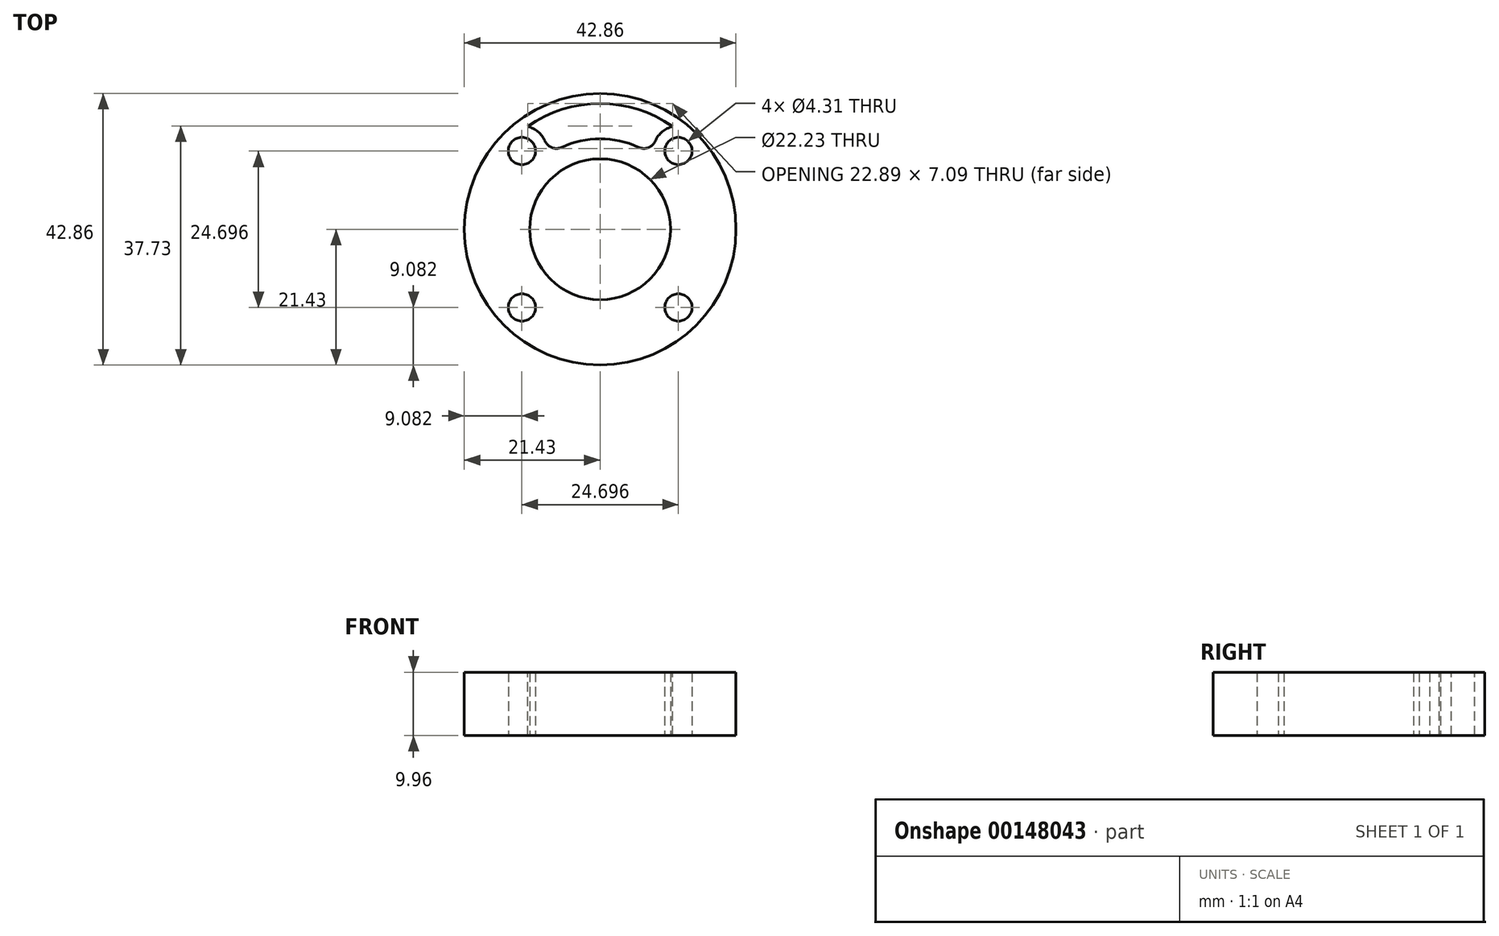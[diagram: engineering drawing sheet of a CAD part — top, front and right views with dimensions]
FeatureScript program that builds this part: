
annotation { "Feature Type Name" : "Feature", "Feature Type Description" : "" }
export const myFeature = defineFeature(function(context is Context, id is Id, definition is map)
    precondition{}
    {
        {
            var Q0;
            Q0=qCreatedBy(makeId("Top.planeOp"),FACE);
            var sketch = newSketch(context, id + "F0", { "sketchPlane" : qUnion([Q0])});
            skCircle(sketch, "E0", {"center": v(0, 0) * mm, "radius": 21.43 * mm});
            skLineSegment(sketch, "E1.bottom", {"start": v(-12.35, 12.35) * mm, "end": v(12.35, 12.35) * mm, "construction": true});
            skLineSegment(sketch, "E1.top", {"start": v(-12.35, -12.35) * mm, "end": v(12.35, -12.35) * mm, "construction": true});
            skLineSegment(sketch, "E1.left", {"start": v(-12.35, 12.35) * mm, "end": v(-12.35, -12.35) * mm, "construction": true});
            skLineSegment(sketch, "E1.right", {"start": v(12.35, 12.35) * mm, "end": v(12.35, -12.35) * mm, "construction": true});
            skCircle(sketch, "E2", {"center": v(-12.35, 12.35) * mm, "radius": 3.97 * mm, "construction": true});
            skCircle(sketch, "E3", {"center": v(12.35, 12.35) * mm, "radius": 2.15 * mm});
            skCircle(sketch, "E4", {"center": v(-12.35, 12.35) * mm, "radius": 2.15 * mm});
            skCircle(sketch, "E5", {"center": v(-12.35, -12.35) * mm, "radius": 2.15 * mm});
            skCircle(sketch, "E6", {"center": v(12.35, -12.35) * mm, "radius": 2.15 * mm});
            skCircle(sketch, "E7", {"center": v(0, 0) * mm, "radius": 11.11 * mm});
            skSolve(sketch);
        }
        {
            var Q0;
            Q0=qSketchRegion(id+"F0",true);
            extrude(context, id + "F1", {"entities" : qUnion([Q0]), "depth" : 9.96 * mm});
        }
        {
            var Q0;
            Q0=makeQuery(id+"F1.opExtrude","CAP_FACE",FACE,{"disambiguationData":[OSD([sQuery(id+"F0.wireOp",EDGE,"E0"),sQuery(id+"F0.wireOp",EDGE,"E3"),sQuery(id+"F0.wireOp",EDGE,"E4"),sQuery(id+"F0.wireOp",EDGE,"E5"),sQuery(id+"F0.wireOp",EDGE,"E6"),sQuery(id+"F0.wireOp",EDGE,"E7")])],"isStart":false});
            var sketch = newSketch(context, id + "F2", { "sketchPlane" : qUnion([Q0])});
            skArc(sketch, "E8", {"start": v(11.44, 16.21) * mm, "mid": v(0, 19.84) * mm, "end": v(-11.44, 16.21) * mm});
            skArc(sketch, "E9", {"start": v(8.47, 11.5) * mm, "mid": v(0, 14.29) * mm, "end": v(-8.47, 11.5) * mm});
            skArc(sketch, "E10", {"start": v(-8.47, 11.5) * mm, "mid": v(-9, 14.47) * mm, "end": v(-11.44, 16.21) * mm});
            skArc(sketch, "E11", {"start": v(11.44, 16.21) * mm, "mid": v(9, 14.47) * mm, "end": v(8.47, 11.5) * mm});
            skSolve(sketch);
        }
        {
            var Q0;
            Q0=qSketchRegion(id+"F2",true);
            var Q1;
            Q1=makeQuery(id+"F1.opExtrude","CAP_FACE",FACE,{"disambiguationData":[OSD([sQuery(id+"F0.wireOp",EDGE,"E0"),sQuery(id+"F0.wireOp",EDGE,"E3"),sQuery(id+"F0.wireOp",EDGE,"E4"),sQuery(id+"F0.wireOp",EDGE,"E5"),sQuery(id+"F0.wireOp",EDGE,"E6"),sQuery(id+"F0.wireOp",EDGE,"E7")])],"isStart":true});
            extrude(context, id + "F3", {"entities" : qUnion([Q0]), "operationType" : NewBodyOperationType.REMOVE, "endBound" : BoundingType.UP_TO_SURFACE, "oppositeDirection" : true, "endBoundEntityFace" : qUnion([Q1]), "depth" : 25.4 * mm});
        }
        {
            var Q0;
            Q0=makeQuery(id+"F3.boolean.opBoolean","COPY",EDGE,{"derivedFrom":makeQuery(id+"F3.opExtrude","SWEPT_EDGE",EDGE,{"disambiguationData":[OSD([sQuery(id+"F2.wireOp",EDGE,"E9"),sQuery(id+"F2.wireOp",EDGE,"E11")])]})});
            var Q1;
            Q1=makeQuery(id+"FQVfpFcfg0FIIHL_1.1.F3.boolean.opBoolean","COPY",EDGE,{"derivedFrom":makeQuery(id+"FQVfpFcfg0FIIHL_1.1.F3.opExtrude","SWEPT_EDGE",EDGE,{"disambiguationData":[OSD([sQuery(id+"F2.wireOp",EDGE,"E9"),sQuery(id+"F2.wireOp",EDGE,"E10")])]})});
            var Q2;
            Q2=makeQuery(id+"FQVfpFcfg0FIIHL_1.1.F3.boolean.opBoolean","COPY",EDGE,{"derivedFrom":makeQuery(id+"FQVfpFcfg0FIIHL_1.1.F3.opExtrude","SWEPT_EDGE",EDGE,{"disambiguationData":[OSD([sQuery(id+"F2.wireOp",EDGE,"E9"),sQuery(id+"F2.wireOp",EDGE,"E11")])]})});
            var Q3;
            Q3=makeQuery(id+"FQVfpFcfg0FIIHL_1.2.F3.boolean.opBoolean","COPY",EDGE,{"derivedFrom":makeQuery(id+"FQVfpFcfg0FIIHL_1.2.F3.opExtrude","SWEPT_EDGE",EDGE,{"disambiguationData":[OSD([sQuery(id+"F2.wireOp",EDGE,"E9"),sQuery(id+"F2.wireOp",EDGE,"E10")])]})});
            var Q4;
            Q4=makeQuery(id+"FQVfpFcfg0FIIHL_1.2.F3.boolean.opBoolean","COPY",EDGE,{"derivedFrom":makeQuery(id+"FQVfpFcfg0FIIHL_1.2.F3.opExtrude","SWEPT_EDGE",EDGE,{"disambiguationData":[OSD([sQuery(id+"F2.wireOp",EDGE,"E9"),sQuery(id+"F2.wireOp",EDGE,"E11")])]})});
            var Q5;
            Q5=makeQuery(id+"FQVfpFcfg0FIIHL_1.3.F3.boolean.opBoolean","COPY",EDGE,{"derivedFrom":makeQuery(id+"FQVfpFcfg0FIIHL_1.3.F3.opExtrude","SWEPT_EDGE",EDGE,{"disambiguationData":[OSD([sQuery(id+"F2.wireOp",EDGE,"E9"),sQuery(id+"F2.wireOp",EDGE,"E10")])]})});
            var Q6;
            Q6=makeQuery(id+"FQVfpFcfg0FIIHL_1.3.F3.boolean.opBoolean","COPY",EDGE,{"derivedFrom":makeQuery(id+"FQVfpFcfg0FIIHL_1.3.F3.opExtrude","SWEPT_EDGE",EDGE,{"disambiguationData":[OSD([sQuery(id+"F2.wireOp",EDGE,"E9"),sQuery(id+"F2.wireOp",EDGE,"E11")])]})});
            var Q7;
            Q7=makeQuery(id+"F3.boolean.opBoolean","COPY",EDGE,{"derivedFrom":makeQuery(id+"F3.opExtrude","SWEPT_EDGE",EDGE,{"disambiguationData":[OSD([sQuery(id+"F2.wireOp",EDGE,"E9"),sQuery(id+"F2.wireOp",EDGE,"E10")])]})});
            fillet(context, id + "F4", {"entities" : qUnion([Q0, Q1, Q2, Q3, Q4, Q5, Q6, Q7]), "radius" : 1.98 * mm, "tangentPropagation" : true, "allowEdgeOverflow" : false});
        }
    });
